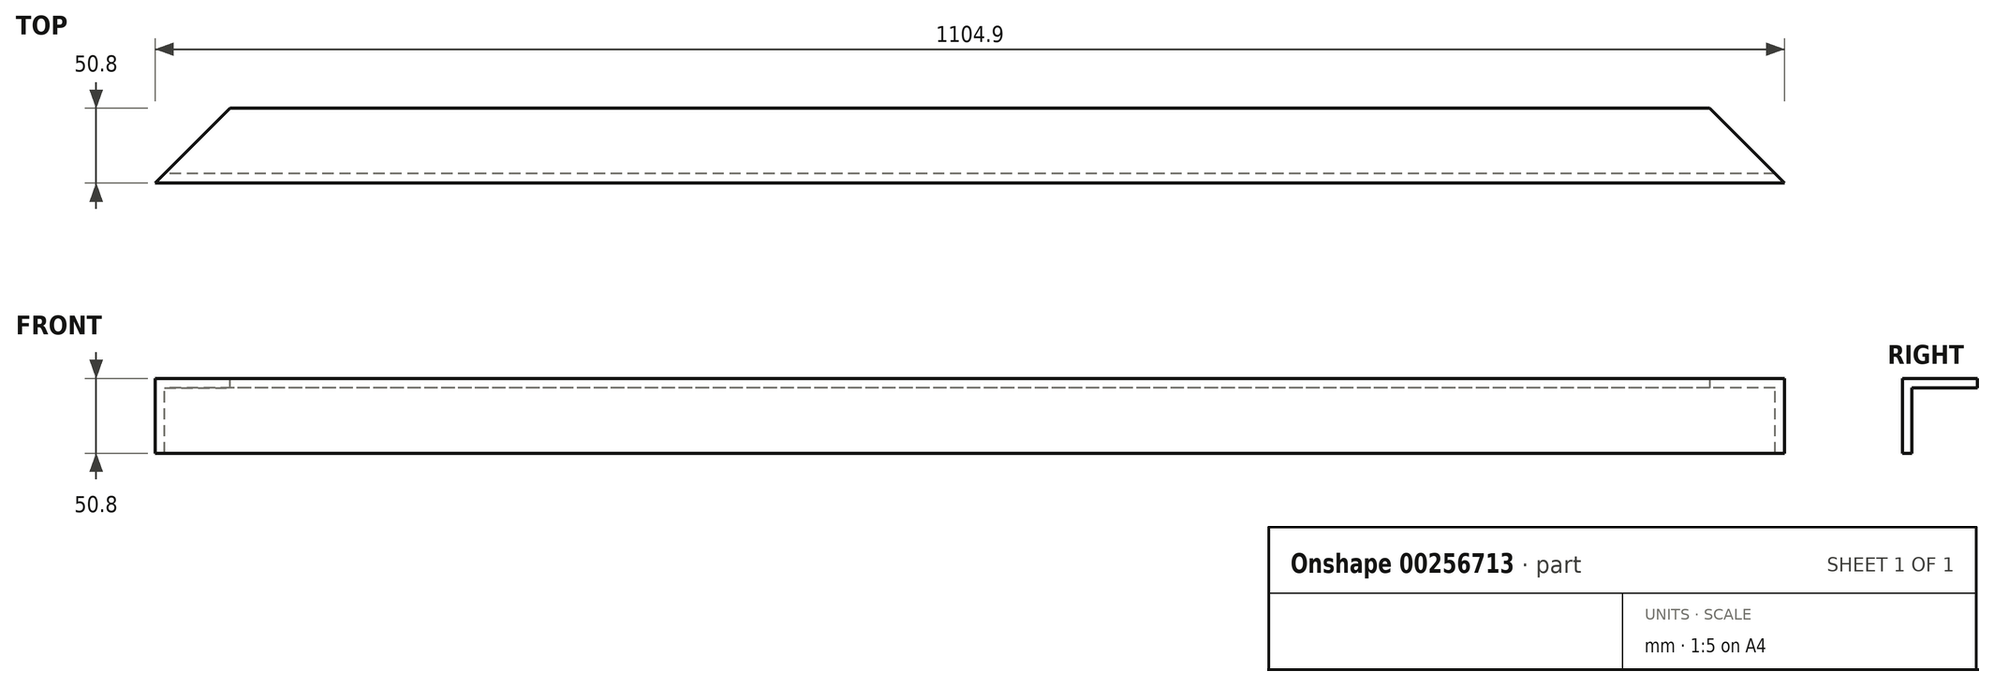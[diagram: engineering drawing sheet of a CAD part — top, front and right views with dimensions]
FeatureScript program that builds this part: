
annotation { "Feature Type Name" : "Feature", "Feature Type Description" : "" }
export const myFeature = defineFeature(function(context is Context, id is Id, definition is map)
    precondition{}
    {
        {
            var Q0;
            Q0=qCreatedBy(makeId("Right.planeOp"),FACE);
            var sketch = newSketch(context, id + "F0", { "sketchPlane" : qUnion([Q0])});
            skLineSegment(sketch, "E0", {"start": v(-24.65, -32.5) * mm, "end": v(-31, -32.5) * mm});
            skLineSegment(sketch, "E1", {"start": v(-31, -32.5) * mm, "end": v(-31, 18.3) * mm});
            skLineSegment(sketch, "E2", {"start": v(-31, 18.3) * mm, "end": v(19.8, 18.3) * mm});
            skLineSegment(sketch, "E3", {"start": v(19.8, 18.3) * mm, "end": v(19.8, 11.94) * mm});
            skLineSegment(sketch, "E4", {"start": v(19.8, 11.94) * mm, "end": v(-24.65, 11.94) * mm});
            skLineSegment(sketch, "E5", {"start": v(-24.65, -32.5) * mm, "end": v(-24.65, 11.94) * mm});
            skSolve(sketch);
        }
        {
            var Q0;
            Q0=makeQuery(id+"F0.imprint","IMPRINT",FACE,{"disambiguationData":[TD([[makeQuery(id+"F0.imprint","IMPRINT",EDGE,{"derivedFrom":sQuery(id+"F0.wireOp",EDGE,"E0")}),-1.0]])]});
            extrude(context, id + "F1", {"entities" : qUnion([Q0]), "depth" : 1104.9 * mm});
        }
        {
            var Q0;
            Q0=makeQuery(id+"F1.opExtrude","CAP_EDGE",EDGE,{"disambiguationData":[OSD([sQuery(id+"F0.wireOp",EDGE,"E3")])],"isStart":false});
            var Q1;
            Q1=makeQuery(id+"F1.opExtrude","CAP_EDGE",EDGE,{"disambiguationData":[OSD([sQuery(id+"F0.wireOp",EDGE,"E3")])],"isStart":true});
            chamfer(context, id + "F2", {"entities" : qUnion([Q0, Q1]), "chamferType" : ChamferType.OFFSET_ANGLE, "width" : 50.8 * mm, "oppositeDirection" : false, "angle" : 45 * degree, "tangentPropagation" : true});
        }
    });
